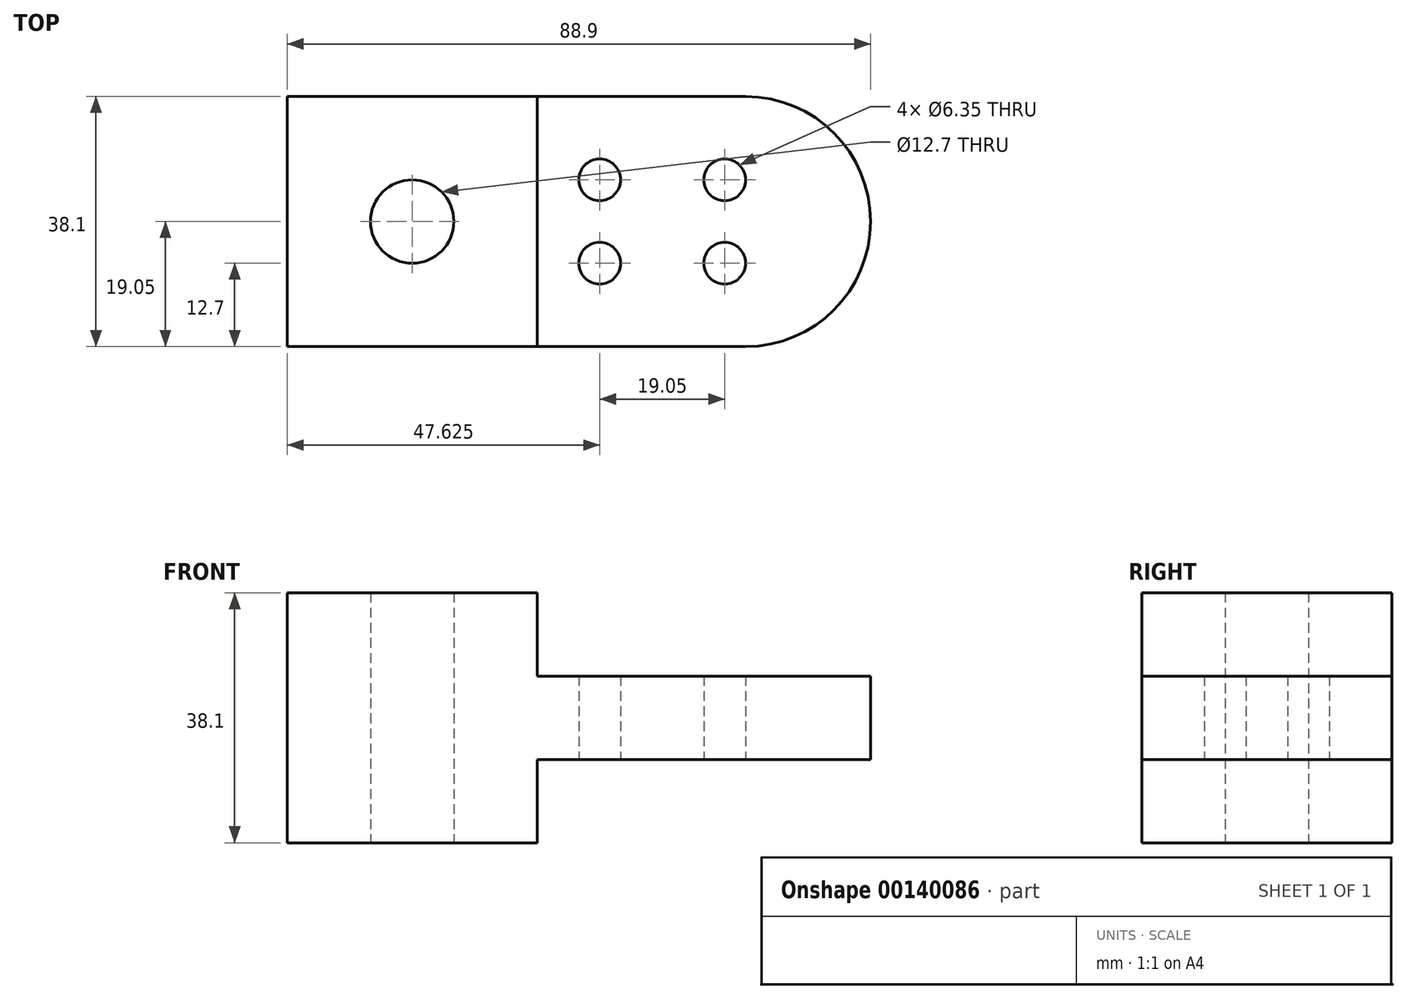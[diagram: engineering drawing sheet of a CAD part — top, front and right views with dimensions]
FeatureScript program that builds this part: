
annotation { "Feature Type Name" : "Feature", "Feature Type Description" : "" }
export const myFeature = defineFeature(function(context is Context, id is Id, definition is map)
    precondition{}
    {
        {
            var Q0;
            Q0=qCreatedBy(makeId("Top.planeOp"),FACE);
            var sketch = newSketch(context, id + "F0", { "sketchPlane" : qUnion([Q0])});
            skLineSegment(sketch, "E0.bottom", {"start": v(0, 0) * mm, "end": v(38.1, 0) * mm});
            skLineSegment(sketch, "E0.top", {"start": v(0, 38.1) * mm, "end": v(38.1, 38.1) * mm});
            skLineSegment(sketch, "E0.left", {"start": v(0, 0) * mm, "end": v(0, 38.1) * mm});
            skLineSegment(sketch, "E0.right", {"start": v(38.1, 0) * mm, "end": v(38.1, 38.1) * mm});
            skLineSegment(sketch, "E1", {"start": v(38.1, 38.1) * mm, "end": v(69.85, 38.1) * mm});
            skLineSegment(sketch, "E2", {"start": v(38.1, 0) * mm, "end": v(69.85, 0) * mm});
            skArc(sketch, "E3", {"start": v(69.85, 0) * mm, "mid": v(88.9, 19.05) * mm, "end": v(69.85, 38.1) * mm});
            skLineSegment(sketch, "E4", {"start": v(19.05, 38.1) * mm, "end": v(19.05, 0) * mm, "construction": true});
            skLineSegment(sketch, "E5", {"start": v(0, 19.05) * mm, "end": v(38.1, 19.05) * mm, "construction": true});
            skCircle(sketch, "E6", {"center": v(19.05, 19.05) * mm, "radius": 6.35 * mm});
            skLineSegment(sketch, "E7", {"start": v(47.63, 38.1) * mm, "end": v(47.63, 0) * mm, "construction": true});
            skLineSegment(sketch, "E8", {"start": v(66.68, 38.1) * mm, "end": v(66.68, 0) * mm, "construction": true});
            skLineSegment(sketch, "E9", {"start": v(38.1, 25.4) * mm, "end": v(69.85, 25.4) * mm, "construction": true});
            skLineSegment(sketch, "E10", {"start": v(38.1, 12.7) * mm, "end": v(66.68, 12.7) * mm, "construction": true});
            skCircle(sketch, "E11", {"center": v(66.68, 12.7) * mm, "radius": 3.18 * mm});
            skCircle(sketch, "E12", {"center": v(47.63, 12.7) * mm, "radius": 3.18 * mm});
            skCircle(sketch, "E13", {"center": v(47.63, 25.4) * mm, "radius": 3.18 * mm});
            skCircle(sketch, "E14", {"center": v(66.68, 25.4) * mm, "radius": 3.18 * mm});
            skSolve(sketch);
        }
        {
            var Q0;
            Q0 = qSketchRegion(id + "F0", true);
            extrude(context, id + "F1", {"entities" : qUnion([Q0]), "depth" : 38.1 * mm});
        }
        {
            var Q0;
            Q0=qCreatedBy(makeId("Front.planeOp"),FACE);
            var sketch = newSketch(context, id + "F2", { "sketchPlane" : qUnion([Q0])});
            skLineSegment(sketch, "E15.bottom", {"start": v(38.1, 38.1) * mm, "end": v(88.9, 38.1) * mm});
            skLineSegment(sketch, "E15.top", {"start": v(38.1, 25.4) * mm, "end": v(88.9, 25.4) * mm});
            skLineSegment(sketch, "E15.left", {"start": v(38.1, 38.1) * mm, "end": v(38.1, 25.4) * mm});
            skLineSegment(sketch, "E15.right", {"start": v(88.9, 38.1) * mm, "end": v(88.9, 25.4) * mm});
            skLineSegment(sketch, "E16.bottom", {"start": v(0, 0) * mm, "end": v(38.1, 0) * mm});
            skLineSegment(sketch, "E16.top", {"start": v(0, 38.1) * mm, "end": v(38.1, 38.1) * mm});
            skLineSegment(sketch, "E16.left", {"start": v(0, 0) * mm, "end": v(0, 38.1) * mm});
            skLineSegment(sketch, "E16.right", {"start": v(38.1, 0) * mm, "end": v(38.1, 38.1) * mm});
            skLineSegment(sketch, "E17.bottom", {"start": v(38.1, 0) * mm, "end": v(88.9, 0) * mm});
            skLineSegment(sketch, "E17.top", {"start": v(38.1, 12.7) * mm, "end": v(88.9, 12.7) * mm});
            skLineSegment(sketch, "E17.left", {"start": v(38.1, 0) * mm, "end": v(38.1, 12.7) * mm});
            skLineSegment(sketch, "E17.right", {"start": v(88.9, 0) * mm, "end": v(88.9, 12.7) * mm});
            skSolve(sketch);
        }
        {
            var Q0;
            {var subQ0=sQuery(id+"F2.wireOp",EDGE,"E15.bottom");Q0=makeQuery(id+"F2.imprint","IMPRINT",FACE,{"disambiguationData":[TD([[makeQuery(id+"F2.imprint","IMPRINT",EDGE,{"derivedFrom":subQ0}),-1.0]])]});}
            var Q1;
            Q1=makeQuery(id+"F2.imprint","IMPRINT",FACE,{"disambiguationData":[TD([[makeQuery(id+"F2.imprint","IMPRINT",EDGE,{"derivedFrom":sQuery(id+"F2.wireOp",EDGE,"E17.bottom")}),1.0]])]});
            extrude(context, id + "F3", {"entities" : qUnion([Q0, Q1]), "operationType" : NewBodyOperationType.REMOVE, "oppositeDirection" : true, "depth" : 38.1 * mm});
        }
    });
